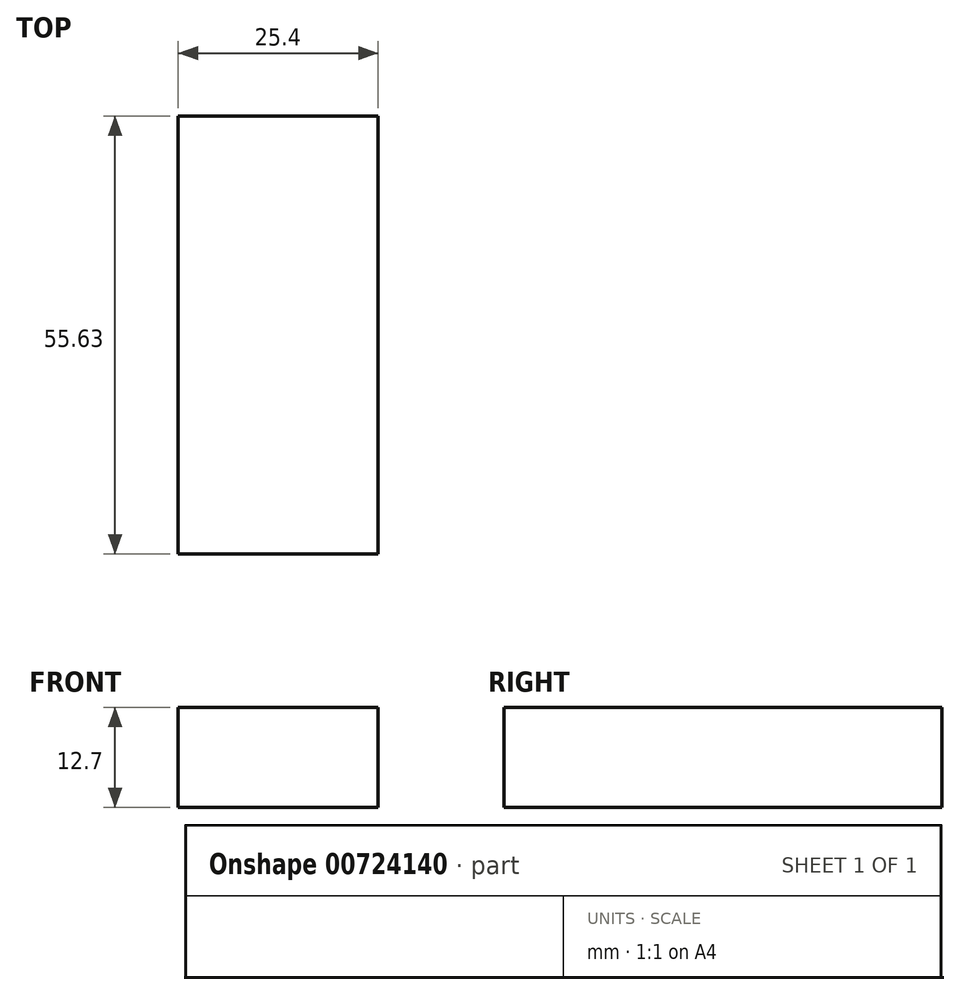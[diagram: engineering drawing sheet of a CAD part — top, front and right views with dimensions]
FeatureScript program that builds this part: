
annotation { "Feature Type Name" : "Feature", "Feature Type Description" : "" }
export const myFeature = defineFeature(function(context is Context, id is Id, definition is map)
    precondition{}
    {
        {
            var Q0;
            Q0=qCreatedBy(makeId("Top.planeOp"),FACE);
            var sketch = newSketch(context, id + "F0", { "sketchPlane" : qUnion([Q0])});
            skLineSegment(sketch, "E0.bottom", {"start": v(0, 0) * mm, "end": v(25.4, 0) * mm});
            skLineSegment(sketch, "E0.top", {"start": v(0, 55.63) * mm, "end": v(25.4, 55.63) * mm});
            skLineSegment(sketch, "E0.left", {"start": v(0, 0) * mm, "end": v(0, 55.63) * mm});
            skLineSegment(sketch, "E0.right", {"start": v(25.4, 0) * mm, "end": v(25.4, 55.63) * mm});
            skSolve(sketch);
        }
        {
            var Q0;
            Q0=makeQuery(id+"F0.imprint","IMPRINT",FACE,{"disambiguationData":[TD([[makeQuery(id+"F0.imprint","IMPRINT",EDGE,{"derivedFrom":sQuery(id+"F0.wireOp",EDGE,"E0.bottom")}),1.0]])]});
            extrude(context, id + "F1", {"entities" : qUnion([Q0]), "depth" : 12.7 * mm, "offsetDistance" : 25.4 * mm});
        }
    });
